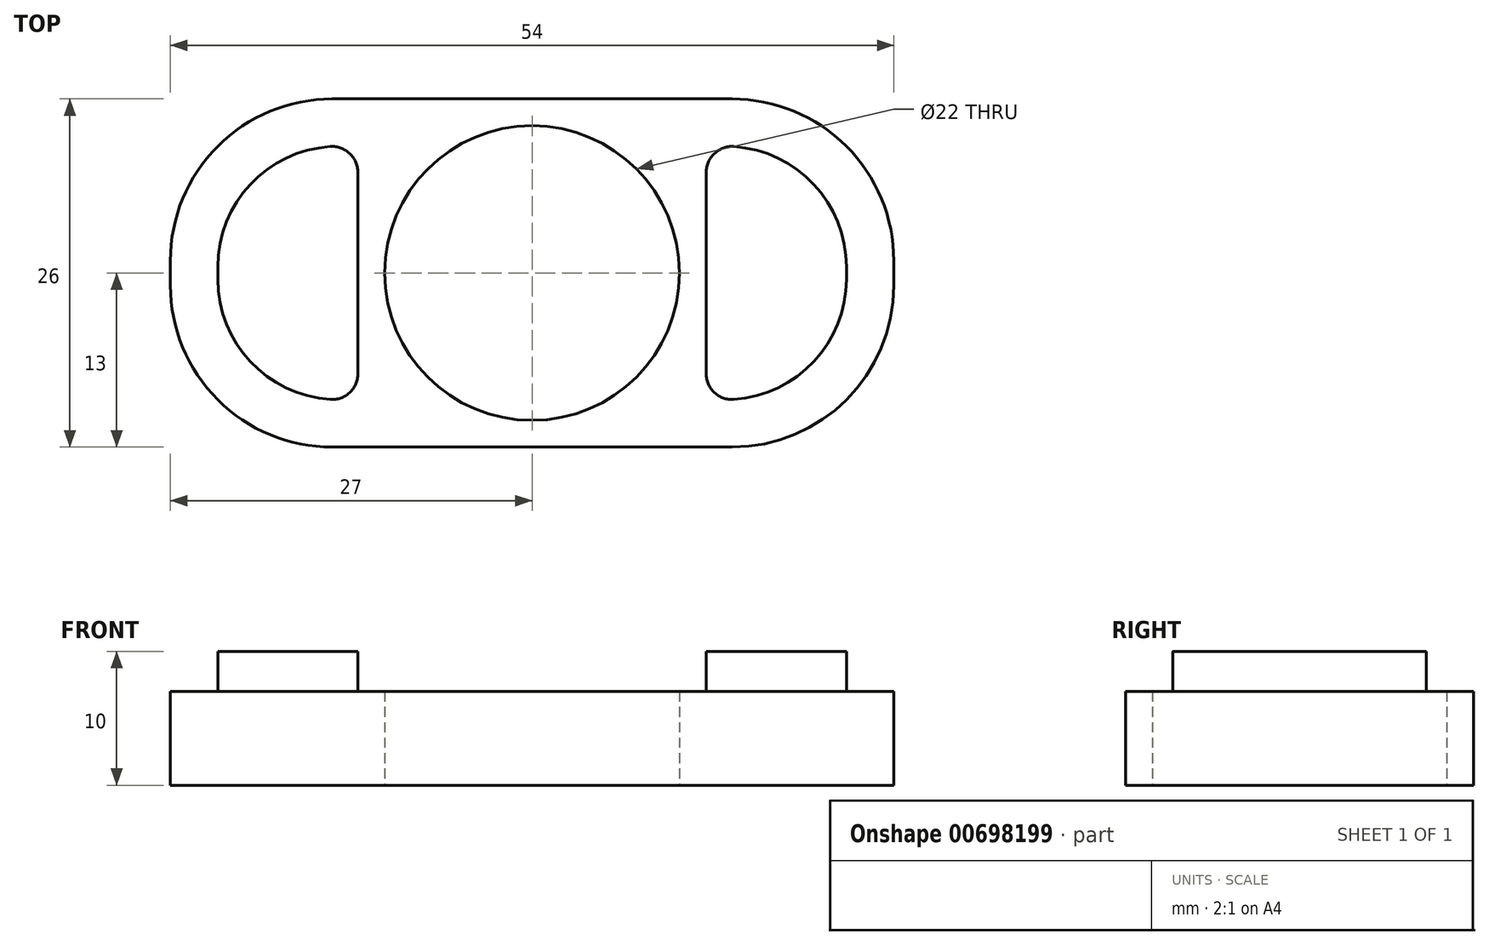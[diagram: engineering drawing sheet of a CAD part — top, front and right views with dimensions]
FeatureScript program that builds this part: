
annotation { "Feature Type Name" : "Feature", "Feature Type Description" : "" }
export const myFeature = defineFeature(function(context is Context, id is Id, definition is map)
    precondition{}
    {
        {
            var Q0;
            Q0=qCreatedBy(makeId("Top.planeOp"),FACE);
            var sketch = newSketch(context, id + "F0", { "sketchPlane" : qUnion([Q0])});
            skCircle(sketch, "E0", {"center": v(0, 0) * mm, "radius": 11 * mm});
            skLineSegment(sketch, "E1.bottom", {"start": v(-27, 13) * mm, "end": v(27, 13) * mm});
            skLineSegment(sketch, "E1.top", {"start": v(-27, -13) * mm, "end": v(27, -13) * mm});
            skLineSegment(sketch, "E1.left", {"start": v(-27, 13) * mm, "end": v(-27, -13) * mm});
            skLineSegment(sketch, "E1.right", {"start": v(27, 13) * mm, "end": v(27, -13) * mm});
            skSolve(sketch);
        }
        {
            var Q0;
            Q0 = qSketchRegion(id + "F0", true);
            extrude(context, id + "F1", {"entities" : qUnion([Q0]), "depth" : 7 * mm, "offsetDistance" : 25 * mm});
        }
        {
            var Q0;
            Q0=makeQuery(id+"F1.opExtrude","SWEPT_EDGE",EDGE,{"disambiguationData":[OSD([sQuery(id+"F0.wireOp",EDGE,"E1.top"),sQuery(id+"F0.wireOp",EDGE,"E1.left")])]});
            var Q1;
            Q1=makeQuery(id+"F1.opExtrude","SWEPT_EDGE",EDGE,{"disambiguationData":[OSD([sQuery(id+"F0.wireOp",EDGE,"E1.bottom"),sQuery(id+"F0.wireOp",EDGE,"E1.left")])]});
            var Q2;
            Q2=makeQuery(id+"F1.opExtrude","SWEPT_EDGE",EDGE,{"disambiguationData":[OSD([sQuery(id+"F0.wireOp",EDGE,"E1.top"),sQuery(id+"F0.wireOp",EDGE,"E1.right")])]});
            var Q3;
            Q3=makeQuery(id+"F1.opExtrude","SWEPT_EDGE",EDGE,{"disambiguationData":[OSD([sQuery(id+"F0.wireOp",EDGE,"E1.bottom"),sQuery(id+"F0.wireOp",EDGE,"E1.right")])]});
            fillet(context, id + "F2", {"entities" : qUnion([Q0, Q1, Q2, Q3]), "radius" : 12.07 * mm, "tangentPropagation" : true, "allowEdgeOverflow" : false});
        }
        {
            var Q0;
            Q0=makeQuery(id+"F1.opExtrude","CAP_FACE",FACE,{"disambiguationData":[OSD([sQuery(id+"F0.wireOp",EDGE,"E0"),sQuery(id+"F0.wireOp",EDGE,"E1.bottom"),sQuery(id+"F0.wireOp",EDGE,"E1.top"),sQuery(id+"F0.wireOp",EDGE,"E1.left"),sQuery(id+"F0.wireOp",EDGE,"E1.right")])],"isStart":false});
            var sketch = newSketch(context, id + "F3", { "sketchPlane" : qUnion([Q0])});
            skLineSegment(sketch, "E2.bottom", {"start": v(-23.46, 9.46) * mm, "end": v(-13, 9.46) * mm});
            skLineSegment(sketch, "E2.top", {"start": v(-23.46, -9.46) * mm, "end": v(-13, -9.46) * mm});
            skLineSegment(sketch, "E2.left", {"start": v(-23.46, 9.46) * mm, "end": v(-23.46, -9.46) * mm});
            skLineSegment(sketch, "E2.right", {"start": v(-13, 9.46) * mm, "end": v(-13, -9.46) * mm});
            skLineSegment(sketch, "E3.bottom", {"start": v(23.46, 9.46) * mm, "end": v(13, 9.46) * mm});
            skLineSegment(sketch, "E3.top", {"start": v(23.46, -9.46) * mm, "end": v(13, -9.46) * mm});
            skLineSegment(sketch, "E3.left", {"start": v(23.46, 9.46) * mm, "end": v(23.46, -9.46) * mm});
            skLineSegment(sketch, "E3.right", {"start": v(13, 9.46) * mm, "end": v(13, -9.46) * mm});
            skSolve(sketch);
        }
        {
            var Q0;
            Q0 = qSketchRegion(id + "F3", true);
            extrude(context, id + "F4", {"entities" : qUnion([Q0]), "operationType" : NewBodyOperationType.ADD, "depth" : 3 * mm, "offsetDistance" : 25 * mm});
        }
        {
            var Q0;
            Q0=makeQuery(id+"F4.opExtrude","SWEPT_EDGE",EDGE,{"disambiguationData":[OSD([sQuery(id+"F3.wireOp",EDGE,"E2.top"),sQuery(id+"F3.wireOp",EDGE,"E2.left")])]});
            var Q1;
            Q1=makeQuery(id+"F4.opExtrude","SWEPT_EDGE",EDGE,{"disambiguationData":[OSD([sQuery(id+"F3.wireOp",EDGE,"E3.top"),sQuery(id+"F3.wireOp",EDGE,"E3.left")])]});
            var Q2;
            Q2=makeQuery(id+"F4.opExtrude","SWEPT_EDGE",EDGE,{"disambiguationData":[OSD([sQuery(id+"F0.wireOp",EDGE,"E0"),sQuery(id+"F0.wireOp",EDGE,"E1.bottom"),sQuery(id+"F0.wireOp",EDGE,"E1.top"),sQuery(id+"F0.wireOp",EDGE,"E1.left"),sQuery(id+"F0.wireOp",EDGE,"E1.right"),sQuery(id+"F3.wireOp",EDGE,"E2.bottom"),sQuery(id+"F3.wireOp",EDGE,"E2.left")])]});
            var Q3;
            Q3=makeQuery(id+"F4.opExtrude","SWEPT_EDGE",EDGE,{"disambiguationData":[OSD([sQuery(id+"F0.wireOp",EDGE,"E0"),sQuery(id+"F0.wireOp",EDGE,"E1.bottom"),sQuery(id+"F0.wireOp",EDGE,"E1.top"),sQuery(id+"F0.wireOp",EDGE,"E1.left"),sQuery(id+"F0.wireOp",EDGE,"E1.right"),sQuery(id+"F3.wireOp",EDGE,"E3.bottom"),sQuery(id+"F3.wireOp",EDGE,"E3.left")])]});
            fillet(context, id + "F5", {"entities" : qUnion([Q0, Q1, Q2, Q3]), "radius" : 9 * mm, "tangentPropagation" : true, "allowEdgeOverflow" : false});
        }
        {
            var Q0;
            Q0 = qSketchRegion(id + "F3", true);
            extrude(context, id + "F6", {"entities" : qUnion([Q0]), "operationType" : NewBodyOperationType.ADD, "depth" : 3 * mm, "offsetDistance" : 25 * mm});
        }
        {
            var Q0;
            Q0=makeQuery(id+"F6.opExtrude","SWEPT_EDGE",EDGE,{"disambiguationData":[OSD([sQuery(id+"F0.wireOp",EDGE,"E0"),sQuery(id+"F0.wireOp",EDGE,"E1.bottom"),sQuery(id+"F0.wireOp",EDGE,"E1.top"),sQuery(id+"F0.wireOp",EDGE,"E1.left"),sQuery(id+"F0.wireOp",EDGE,"E1.right"),sQuery(id+"F3.wireOp",EDGE,"E2.bottom"),sQuery(id+"F3.wireOp",EDGE,"E2.left")])]});
            var Q1;
            Q1=makeQuery(id+"F6.opExtrude","SWEPT_EDGE",EDGE,{"disambiguationData":[OSD([sQuery(id+"F3.wireOp",EDGE,"E2.top"),sQuery(id+"F3.wireOp",EDGE,"E2.left")])]});
            var Q2;
            Q2=makeQuery(id+"F6.opExtrude","SWEPT_EDGE",EDGE,{"disambiguationData":[OSD([sQuery(id+"F3.wireOp",EDGE,"E3.top"),sQuery(id+"F3.wireOp",EDGE,"E3.left")])]});
            var Q3;
            Q3=makeQuery(id+"F6.opExtrude","SWEPT_EDGE",EDGE,{"disambiguationData":[OSD([sQuery(id+"F0.wireOp",EDGE,"E0"),sQuery(id+"F0.wireOp",EDGE,"E1.bottom"),sQuery(id+"F0.wireOp",EDGE,"E1.top"),sQuery(id+"F0.wireOp",EDGE,"E1.left"),sQuery(id+"F0.wireOp",EDGE,"E1.right"),sQuery(id+"F3.wireOp",EDGE,"E3.bottom"),sQuery(id+"F3.wireOp",EDGE,"E3.left")])]});
            fillet(context, id + "F7", {"entities" : qUnion([Q0, Q1, Q2, Q3]), "radius" : 9 * mm, "tangentPropagation" : true, "allowEdgeOverflow" : false});
        }
        {
            var Q0;
            Q0=makeQuery(id+"F4.opExtrude","SWEPT_EDGE",EDGE,{"disambiguationData":[OSD([sQuery(id+"F3.wireOp",EDGE,"E3.top"),sQuery(id+"F3.wireOp",EDGE,"E3.right")])]});
            var Q1;
            Q1=makeQuery(id+"F4.opExtrude","SWEPT_EDGE",EDGE,{"disambiguationData":[OSD([sQuery(id+"F3.wireOp",EDGE,"E3.bottom"),sQuery(id+"F3.wireOp",EDGE,"E3.right")])]});
            var Q2;
            Q2=makeQuery(id+"F4.opExtrude","SWEPT_EDGE",EDGE,{"disambiguationData":[OSD([sQuery(id+"F3.wireOp",EDGE,"E2.top"),sQuery(id+"F3.wireOp",EDGE,"E2.right")])]});
            var Q3;
            Q3=makeQuery(id+"F4.opExtrude","SWEPT_EDGE",EDGE,{"disambiguationData":[OSD([sQuery(id+"F3.wireOp",EDGE,"E2.bottom"),sQuery(id+"F3.wireOp",EDGE,"E2.right")])]});
            fillet(context, id + "F8", {"entities" : qUnion([Q0, Q1, Q2, Q3]), "radius" : 1.93 * mm, "tangentPropagation" : true, "allowEdgeOverflow" : false});
        }
    });
